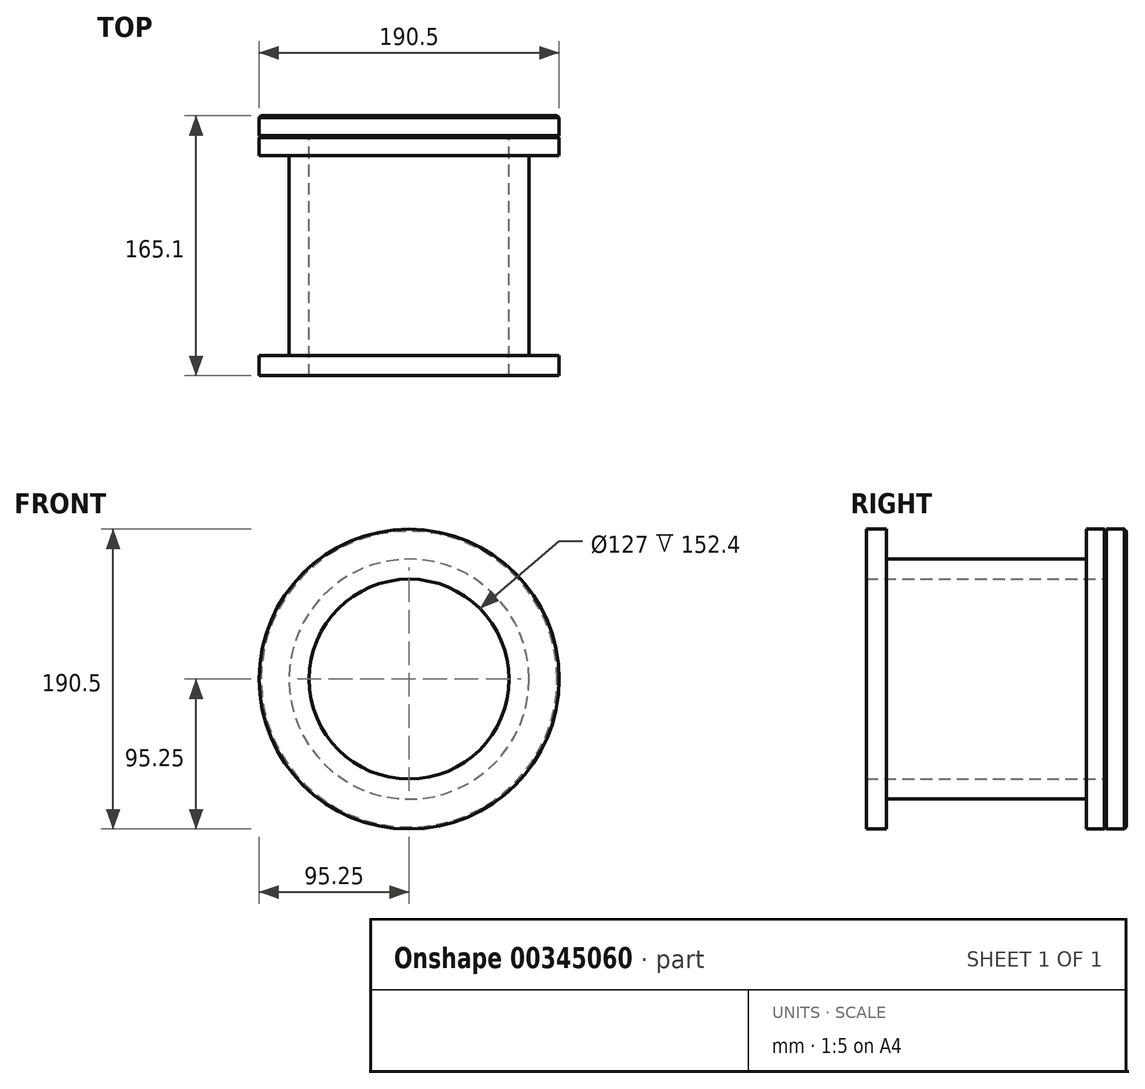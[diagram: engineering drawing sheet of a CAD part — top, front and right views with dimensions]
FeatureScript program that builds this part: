
annotation { "Feature Type Name" : "Feature", "Feature Type Description" : "" }
export const myFeature = defineFeature(function(context is Context, id is Id, definition is map)
    precondition{}
    {
        {
            var Q0;
            Q0=qCreatedBy(makeId("Right.planeOp"),FACE);
            var sketch = newSketch(context, id + "F0", { "sketchPlane" : qUnion([Q0])});
            skLineSegment(sketch, "E0", {"start": v(-52.84, 0) * mm, "end": v(74.16, 0) * mm});
            skSolve(sketch);
        }
        {
            var Q0;
            Q0=sQuery(id+"F0.wireOp",EDGE,"E0");
            var Q1;
            Q1=sQuery(id+"F0.wireOp",VERTEX,"E0.start");
            cPlane(context, id + "F1", {"entities" : qUnion([Q0, Q1]), "cplaneType" : CPlaneType.LINE_POINT, "offset" : 25.4 * mm, "width" : 152.4 * mm, "height" : 152.4 * mm});
        }
        {
            var Q0;
            Q0=qCreatedBy(id+"F1.planeOp",FACE);
            var sketch = newSketch(context, id + "F2", { "sketchPlane" : qUnion([Q0])});
            skCircle(sketch, "E1", {"center": v(0, 0) * mm, "radius": 76.2 * mm});
            skCircle(sketch, "E2", {"center": v(0, 0) * mm, "radius": 95.25 * mm});
            skSolve(sketch);
        }
        {
            var Q0;
            Q0=makeQuery(id+"F2.imprint","IMPRINT",FACE,{"disambiguationData":[TD([[makeQuery(id+"F2.imprint","IMPRINT",EDGE,{"derivedFrom":sQuery(id+"F2.wireOp",EDGE,"E1")}),-1.0]])]});
            var Q1;
            Q1=sQuery(id+"F0.wireOp",EDGE,"E0");
            sweep(context, id + "F3", {"profiles" : qUnion([Q0]), "path" : qUnion([Q1])});
        }
        {
            var Q0;
            Q0=makeQuery(id+"F3.opSweep","SWEPT_FACE",FACE,{"disambiguationData":[OSD([sQuery(id+"F0.wireOp",EDGE,"E0"),sQuery(id+"F2.wireOp",EDGE,"E2")])]});
            shell(context, id + "F4", {"entities" : qUnion([Q0]), "thickness" : 12.7 * mm, "oppositeDirection" : true});
        }
        {
            var Q0;
            Q0=makeQuery(id+"F3.opSweep","CAP_FACE",FACE,{"disambiguationData":[OSD([sQuery(id+"F0.wireOp",VERTEX,"E0.end"),sQuery(id+"F2.wireOp",EDGE,"E1"),sQuery(id+"F2.wireOp",EDGE,"E2")])],"isStart":false});
            cPlane(context, id + "F5", {"entities" : qUnion([Q0]), "cplaneType" : CPlaneType.OFFSET, "offset" : 0 * mm, "width" : 152.4 * mm, "height" : 152.4 * mm});
        }
        {
            var Q0;
            Q0=qCreatedBy(id+"F5.planeOp",FACE);
            var sketch = newSketch(context, id + "F6", { "sketchPlane" : qUnion([Q0])});
            skCircle(sketch, "E3", {"center": v(0, 0) * mm, "radius": 95.25 * mm});
            skSolve(sketch);
        }
        {
            var Q0;
            Q0=makeQuery(id+"F6.imprint","IMPRINT",FACE,{"disambiguationData":[TD([[makeQuery(id+"F6.imprint","IMPRINT",EDGE,{"derivedFrom":sQuery(id+"F6.wireOp",EDGE,"E3")}),1.0]])]});
            extrude(context, id + "F7", {"entities" : qUnion([Q0]), "depth" : 12.7 * mm});
        }
        {
            var Q0;
            Q0=makeQuery(id+"F3.opSweep","CAP_EDGE",EDGE,{"disambiguationData":[OSD([sQuery(id+"F0.wireOp",VERTEX,"E0.end"),sQuery(id+"F2.wireOp",EDGE,"E2")])],"isStart":false});
            var Q1;
            Q1=makeQuery(id+"F7.opExtrude","CAP_EDGE",EDGE,{"disambiguationData":[OSD([sQuery(id+"F6.wireOp",EDGE,"E3")])],"isStart":false});
            chamfer(context, id + "F8", {"entities" : qUnion([Q0, Q1]), "width" : 1.27 * mm, "tangentPropagation" : true});
        }
    });
